# Revit family: OFS_BRANDS_EMBRACE_TABLES
name_source: partatom
category: Furniture Systems
revit_build: Autodesk Revit Architecture 2013 (Build: 20120221_2030(x64)
units: mm (PartAtom-declared; Revit-internal decimal feet)

## types (5) — shared parameters
Assembly Code = E2020200
Catalog = OFS BRANDS http://ofs.com
D2 = 0' - 1 3/16"
Description = OFS BRANDS Embrace Tables
H2 = 0' - 1"
H3 = 0' - 6"
LEG POSITION 2 = 0' - 1 13/16"
LEG POSITION1 = 0' - 0 5/8"
Manufacturer = OFS BRANDS
URL = http://ofsbrands.com
W2 = 0' - 0 13/16"
W3 = 0' - 0 3/8"

## per-type parameters (varying)
| type | D | DIAMETER | DIAMETER2 | H | H LEG | H.R | H.R2 | LEG.P.R1 | LEG.P.R2 | Model | ROUND TABLE | SQUARE TABLE | W |
| RECTANGLE CONSOLE TABLE | 1' - 6" | 1' - 5" | 1' - 4" | 3' - 0" | 2' - 5" | 3' - 0" | 2' - 11" | 1' - 2 5/32" | 1' - 2 5/32" | EFC108-18X60 | No | Yes | 5' - 0" |
| SQUARE END TABLE | 2' - 0" | 1' - 6" | 1' - 5" | 1' - 11" | 1' - 4" | 1' - 6" | 1' - 5" | 1' - 4" | 1' - 4" | EFC108-24SQ | No | Yes | 2' - 0" |
| ROUND COCKTAIL TABLE | 2' - 0" | 2' - 8 3/16" | 2' - 5 1/16" | 1' - 6" | 0' - 11" | 1' - 6" | 1' - 5" | 2' - 3 7/8" | 2' - 3 7/8" | EFC108-32RD | Yes | No | 2' - 0" |
| ROUND END TABLE 24 | 2' - 0" | 2' - 0" | 1' - 9 1/2" | 1' - 11" | 1' - 4" | 1' - 11" | 1' - 10" | 1' - 8 5/32" | 1' - 8 5/32" | EFC108-24RD | Yes | No | 2' - 0" |
| ROUND END TABLE 18 | 2' - 0" | 1' - 6" | 1' - 3 1/2" | 1' - 11" | 1' - 4" | 1' - 11" | 1' - 10" | 1' - 2 5/32" | 1' - 2 5/32" | EFC108-18RD | Yes | No | 2' - 0" |

## geometry (parser evidence)
native form markers: Blend x4, Sweep x1
no freeform markers — native parametric forms only
